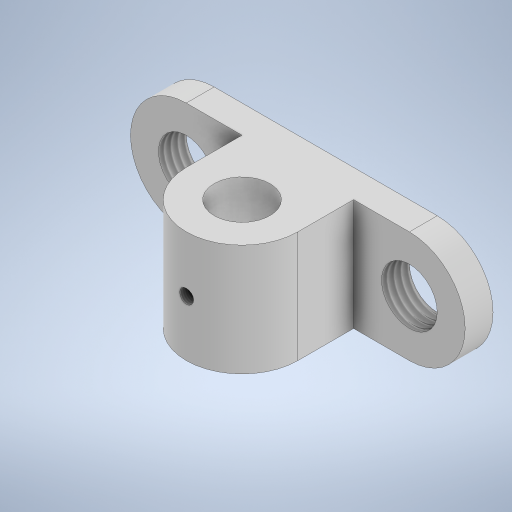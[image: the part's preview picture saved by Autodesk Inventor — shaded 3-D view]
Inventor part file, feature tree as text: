
AUTODESK INVENTOR PART (.ipt)
format: ipt  version: 2024 (Build 280153000, 153)  size: 305,152 bytes
history: native  units: in
note: dims shown in document units (in); Inventor stores cm internally (conversion verified against a paired STEP export)
features: extrude x6, sketch x6, thread x3, plane x1
ambient origin geometry x8: Origin, YZ Plane, XZ Plane, XY Plane, X Axis, Y Axis, Z Axis, Center Point
bodies: Body1 (feature_tree)
feature tree (16):
  extrude  "Extrusion2"  Depth=1.5748in
  extrude  "Extrusion3"  Depth=0.3937in
  extrude  "Extrusion4"  Depth=0.3937in
  extrude  "Extrusion5"  TaperAngle=0.0deg  [1 undecoded]
  extrude  "Extrusion6"  TaperAngle=0.0deg  [1 undecoded]
  plane  "Work Plane1"
  extrude  "Extrusion7"  Depth=0.3937in TaperAngle=0.0deg
  thread  "Thread1"  [1 undecoded]
  thread  "Thread2"  [1 undecoded]
  thread  "Thread3"  [1 undecoded]
  sketch  "Sketch2"  dims[d5=1.5748in d6=1.5748in]
  sketch  "Sketch3"  dims[d7=1.9685in d8=0.0in d9=0.3937in]
  sketch  "Sketch4"  dims[d11=1.5748in d12=0.0in d13=0.3937in]
  sketch  "Sketch5"  dims[d14=1.5748in d15=0.0in d18=0.0in d19=0.0in]
  sketch  "Sketch6"  dims[d20=0.7874in d21=0.0in d22=0.0in]
  sketch  "Sketch8"  dims[d31=0.1969in d32=0.4724in d33=0.0in d34=0.3937in d35=0.0in d36=0.4062in d37=0.0in d38=0.3937in d39=0.0in]
note: 5 required parameter values undecoded (feature->parameter linkage not recoverable at this tier; creation-order binding heuristic only, values carry confidence <= 0.55)
